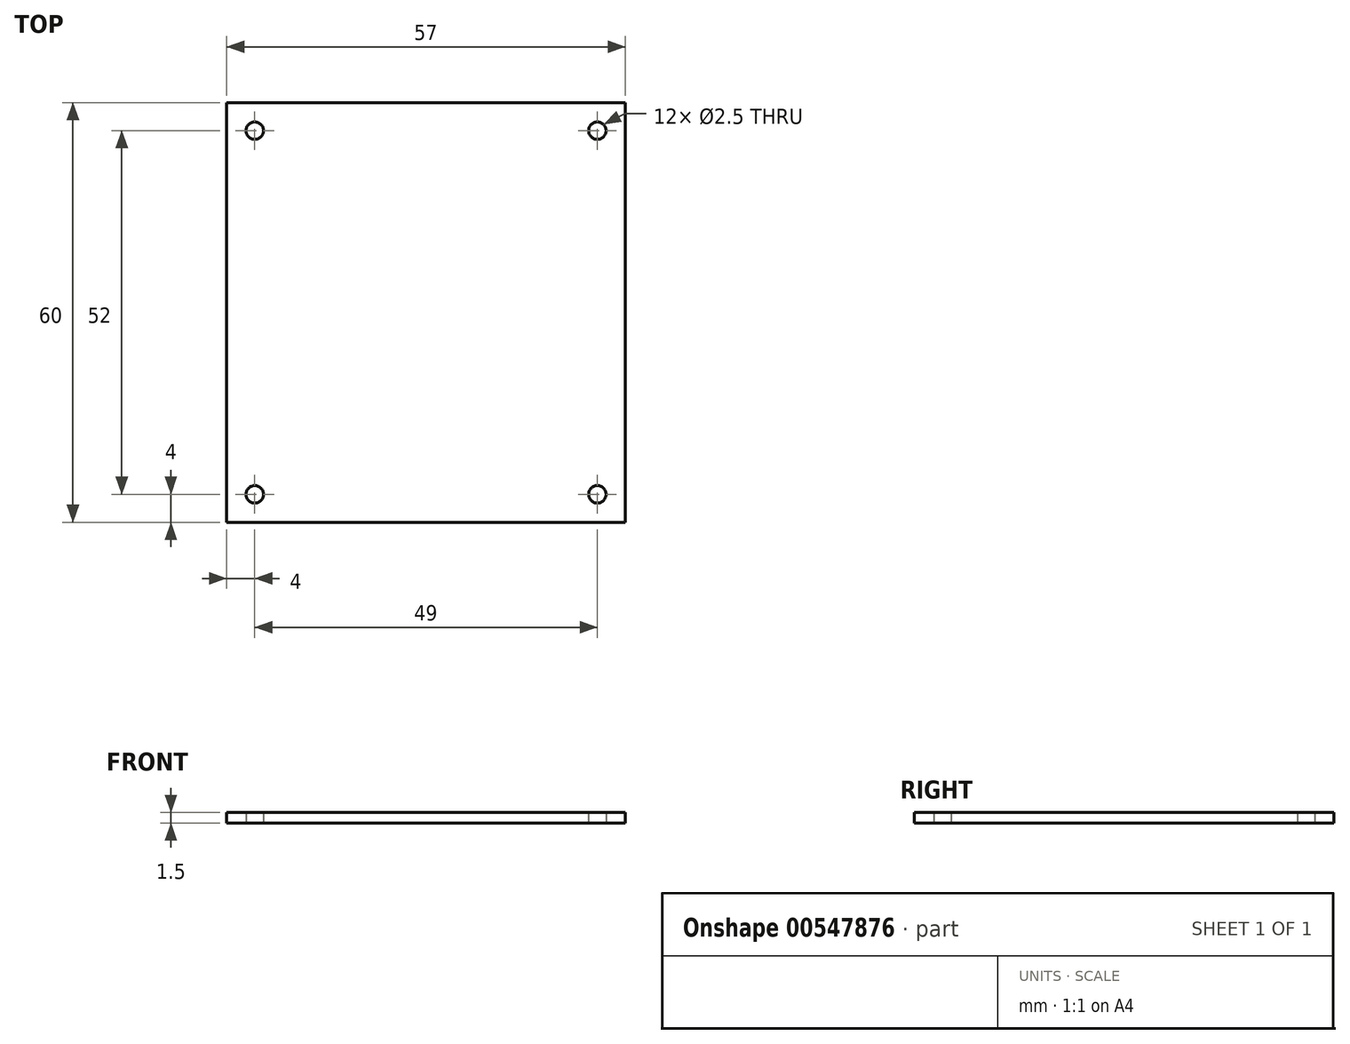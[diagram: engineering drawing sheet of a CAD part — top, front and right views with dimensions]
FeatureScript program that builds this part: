
annotation { "Feature Type Name" : "Feature", "Feature Type Description" : "" }
export const myFeature = defineFeature(function(context is Context, id is Id, definition is map)
    precondition{}
    {
        {
            var Q0;
            Q0=qCreatedBy(makeId("Top.planeOp"),FACE);
            var sketch = newSketch(context, id + "F0", { "sketchPlane" : qUnion([Q0])});
            skLineSegment(sketch, "E0.bottom", {"start": v(28.5, -30) * mm, "end": v(-28.5, -30) * mm});
            skLineSegment(sketch, "E0.top", {"start": v(28.5, 30) * mm, "end": v(-28.5, 30) * mm});
            skLineSegment(sketch, "E0.left", {"start": v(28.5, -30) * mm, "end": v(28.5, 30) * mm});
            skLineSegment(sketch, "E0.right", {"start": v(-28.5, -30) * mm, "end": v(-28.5, 30) * mm});
            skPoint(sketch, "E0.middle", {"position": v(0, 0) * mm});
            skLineSegment(sketch, "E1.bottom", {"start": v(24.5, -26) * mm, "end": v(-24.5, -26) * mm, "construction": true});
            skLineSegment(sketch, "E1.top", {"start": v(24.5, 26) * mm, "end": v(-24.5, 26) * mm, "construction": true});
            skLineSegment(sketch, "E1.left", {"start": v(24.5, -26) * mm, "end": v(24.5, 26) * mm, "construction": true});
            skLineSegment(sketch, "E1.right", {"start": v(-24.5, -26) * mm, "end": v(-24.5, 26) * mm, "construction": true});
            skCircle(sketch, "E2", {"center": v(-24.5, 26) * mm, "radius": 1.25 * mm});
            skCircle(sketch, "E3", {"center": v(24.5, 26) * mm, "radius": 1.25 * mm});
            skCircle(sketch, "E4", {"center": v(24.5, -26) * mm, "radius": 1.25 * mm});
            skCircle(sketch, "E5", {"center": v(-24.5, -26) * mm, "radius": 1.25 * mm});
            skSolve(sketch);
        }
        {
            var Q0;
            Q0=makeQuery(id+"F0.imprint","IMPRINT",FACE,{"disambiguationData":[TD([[makeQuery(id+"F0.imprint","IMPRINT",EDGE,{"derivedFrom":sQuery(id+"F0.wireOp",EDGE,"E0.bottom")}),-1.0]])]});
            extrude(context, id + "F1", {"entities" : qUnion([Q0]), "depth" : 1.5 * mm, "offsetDistance" : 25 * mm});
        }
    });
